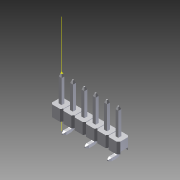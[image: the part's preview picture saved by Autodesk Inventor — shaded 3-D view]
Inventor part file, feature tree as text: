
AUTODESK INVENTOR PART (.ipt)
format: ipt  version: 2015 (Build 190159000, 159)  size: 398,336 bytes
history: native  units: in
note: dims shown in document units (in); Inventor stores cm internally (conversion verified against a paired STEP export)
features: other x5, extrude x1, sketch x1
ambient origin geometry x8: Origin, YZ Plane, XZ Plane, XY Plane, X Axis, Y Axis, Z Axis, Center Point
bodies: Solid1 (feature_tree)
feature tree (7):
  other  "Model_2.ipt1"
  other  "Work Axis1"
  extrude  "Extrusion1"  [1 undecoded]
  other  "Work Point1"
  sketch  "Sketch2"  dims[d0=1.0in d1=0.0in]
  other  "Composite1"
  other  "Srf1"
note: 1 required parameter value undecoded (feature->parameter linkage not recoverable at this tier; creation-order binding heuristic only, values carry confidence <= 0.55)
